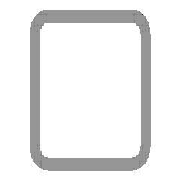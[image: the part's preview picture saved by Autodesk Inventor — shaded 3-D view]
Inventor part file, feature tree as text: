
AUTODESK INVENTOR PART (.ipt)
format: ipt  version: 2025.1 (Build 291241020, 241B)  size: 134,144 bytes
history: native  units: mm (DEFAULTED — no unit token found)
features: other x4, sketch x1, plane x1
ambient origin geometry x8: Origin, YZ Plane, XZ Plane, XY Plane, X Axis, Y Axis, Z Axis, Center Point
bodies: Solid1 (feature_tree), Body (feature_tree)
feature tree (6):
  parser-record x1  (decoder bookkeeping rows leaked as tree rows — omitted from the tree; the rows remain in map.json)
  other  "Driven Length"
  other  "Start Plane"
  other  "End Plane"
  sketch  "Sketch3"  dims[d3=850.0mm d4=0.0mm d7=4.0mm d9=40.0mm d11=40.0mm d12=2.0mm d13=50.0mm d14=900.0mm d15=20.0mm d16=20.0mm d17=90.0deg d18=850.0mm]
  plane  "Work Plane3"
